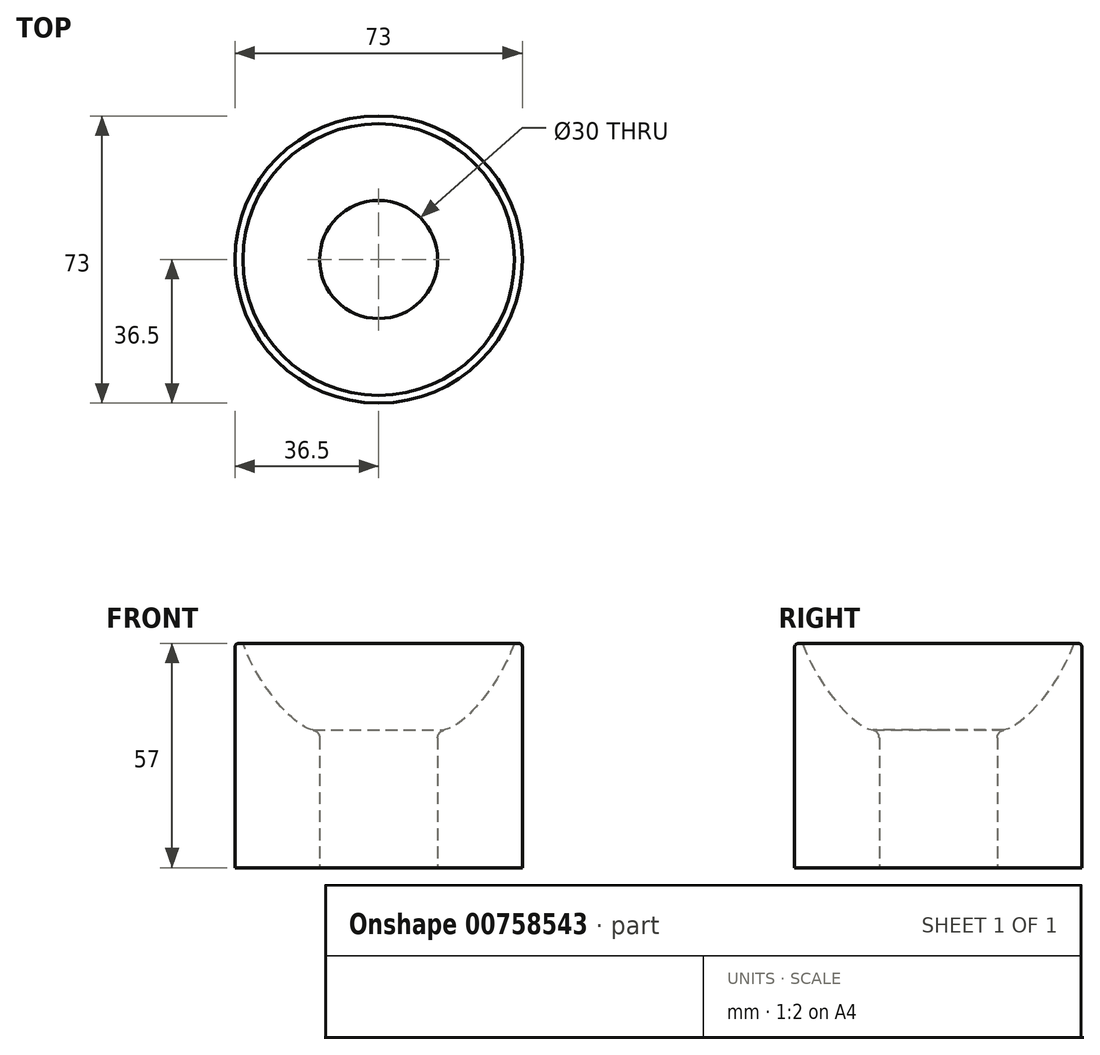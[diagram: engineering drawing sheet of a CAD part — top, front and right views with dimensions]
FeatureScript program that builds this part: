
annotation { "Feature Type Name" : "Feature", "Feature Type Description" : "" }
export const myFeature = defineFeature(function(context is Context, id is Id, definition is map)
    precondition{}
    {
        {
            var Q0;
            Q0=qCreatedBy(makeId("Front.planeOp"),FACE);
            var sketch = newSketch(context, id + "F0", { "sketchPlane" : qUnion([Q0])});
            skLineSegment(sketch, "E0", {"start": v(15, 0) * mm, "end": v(36.5, 0) * mm});
            skLineSegment(sketch, "E1", {"start": v(36.5, 0) * mm, "end": v(36.5, 57) * mm});
            skLineSegment(sketch, "E2", {"start": v(36.5, 57) * mm, "end": v(34.5, 57) * mm});
            skLineSegment(sketch, "E3", {"start": v(15, 35) * mm, "end": v(15, 0) * mm});
            skLineSegment(sketch, "E4", {"start": v(0, 0) * mm, "end": v(0, 38.95) * mm, "construction": true});
            skFitSpline(sketch, "E5", {"points": [v(15, 35) * mm, v(34.5, 57) * mm], "startDerivative": vector(14.36, -4.57) * mm, "endDerivative": vector(12.72, 34.77) * mm});
            skSolve(sketch);
        }
        {
            var Q0;
            Q0=makeQuery(id+"F0.imprint","IMPRINT",FACE,{"disambiguationData":[TD([[makeQuery(id+"F0.imprint","IMPRINT",EDGE,{"derivedFrom":sQuery(id+"F0.wireOp",EDGE,"E0")}),1.0]])]});
            var Q1;
            Q1=sQuery(id+"F0.wireOp",EDGE,"E4");
            revolve(context, id + "F1", {"surfaceOperationType" : NewSurfaceOperationType.NEW, "entities" : qUnion([Q0]), "axis" : qUnion([Q1]), "revolveType" : RevolveType.FULL});
        }
        {
            var Q0;
            Q0=makeQuery(id+"F1.opRevolve","SWEPT_EDGE",EDGE,{"disambiguationData":[OSD([sQuery(id+"F0.wireOp",EDGE,"E3"),sQuery(id+"F0.wireOp",EDGE,"E5")])]});
            fillet(context, id + "F2", {"entities" : qUnion([Q0]), "radius" : 2 * mm, "tangentPropagation" : true, "allowEdgeOverflow" : false});
        }
        {
            var Q0;
            Q0=makeQuery(id+"F1.opRevolve","SWEPT_EDGE",EDGE,{"disambiguationData":[OSD([sQuery(id+"F0.wireOp",EDGE,"E1"),sQuery(id+"F0.wireOp",EDGE,"E2")])]});
            fillet(context, id + "F3", {"entities" : qUnion([Q0]), "radius" : 1 * mm, "tangentPropagation" : true, "allowEdgeOverflow" : false});
        }
    });
